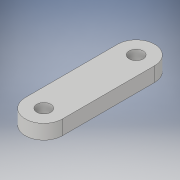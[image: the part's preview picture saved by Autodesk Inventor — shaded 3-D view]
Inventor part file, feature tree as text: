
AUTODESK INVENTOR PART (.ipt)
format: ipt  version: 2019.4 (Build 234330000, 330)  size: 136,192 bytes
history: native  units: mm
features: sketch x5, extrude x2, hole x1, thicken_offset x1
ambient origin geometry x8: Origin, YZ Plane, XZ Plane, XY Plane, X Axis, Y Axis, Z Axis, Center Point
bodies: Solid1 (feature_tree)
feature tree (9):
  extrude  "Extrusion1"  Depth=5.5mm
  sketch  "Sketch2"  dims[d8=34.9mm d9=5.31mm]
  extrude  "Extrusion2"  Depth=34.9mm
  sketch  "Sketch4"  dims[d13=90.0deg]
  sketch  "Sketch5"  dims[d14=34.9mm d15=3.8mm d16=34.9mm d17=3.8mm d18=1.2mm d19=0.0mm d20=5.1mm d21=33.3mm d22=5.31mm d23=2.0mm d24=0.525344mm d25=4.0mm d26=20.594885mm d27=2.0mm d28=2.0mm]
  hole  "Hole1"  [1 undecoded]
  thicken_offset  "Thicken1"
  sketch  "Sketch1"  dims[d5=5.5mm d6=0.0mm d7=5.31mm]
  sketch  "Sketch3"  dims[d11=34.9mm d12=5.0mm]
note: 1 required parameter value undecoded (feature->parameter linkage not recoverable at this tier; creation-order binding heuristic only, values carry confidence <= 0.55)
